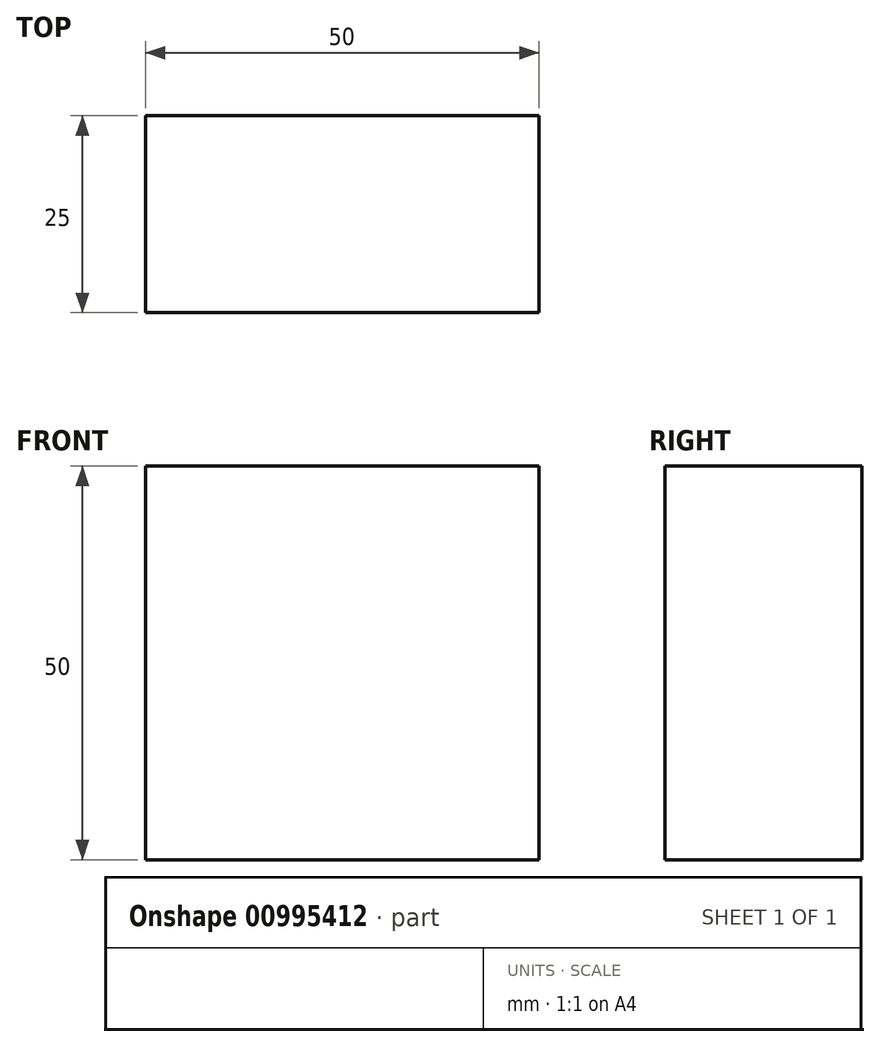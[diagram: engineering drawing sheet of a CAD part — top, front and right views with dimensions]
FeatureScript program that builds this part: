
annotation { "Feature Type Name" : "Feature", "Feature Type Description" : "" }
export const myFeature = defineFeature(function(context is Context, id is Id, definition is map)
    precondition{}
    {
        {
            var Q0;
            Q0=qCreatedBy(makeId("Front.planeOp"),FACE);
            var sketch = newSketch(context, id + "F0", { "sketchPlane" : qUnion([Q0])});
            skLineSegment(sketch, "E0.bottom", {"start": v(25, -25) * mm, "end": v(-25, -25) * mm});
            skLineSegment(sketch, "E0.top", {"start": v(25, 25) * mm, "end": v(-25, 25) * mm});
            skLineSegment(sketch, "E0.left", {"start": v(25, -25) * mm, "end": v(25, 25) * mm});
            skLineSegment(sketch, "E0.right", {"start": v(-25, -25) * mm, "end": v(-25, 25) * mm});
            skPoint(sketch, "E0.middle", {"position": v(0, 0) * mm});
            skSolve(sketch);
        }
        {
            var Q0;
            Q0=makeQuery(id+"F0.imprint","IMPRINT",FACE,{"disambiguationData":[TD([[makeQuery(id+"F0.imprint","IMPRINT",EDGE,{"derivedFrom":sQuery(id+"F0.wireOp",EDGE,"E0.bottom")}),-1.0]])]});
            extrude(context, id + "F1", {"entities" : qUnion([Q0]), "depth" : 25 * mm, "offsetDistance" : 25 * mm});
        }
    });
